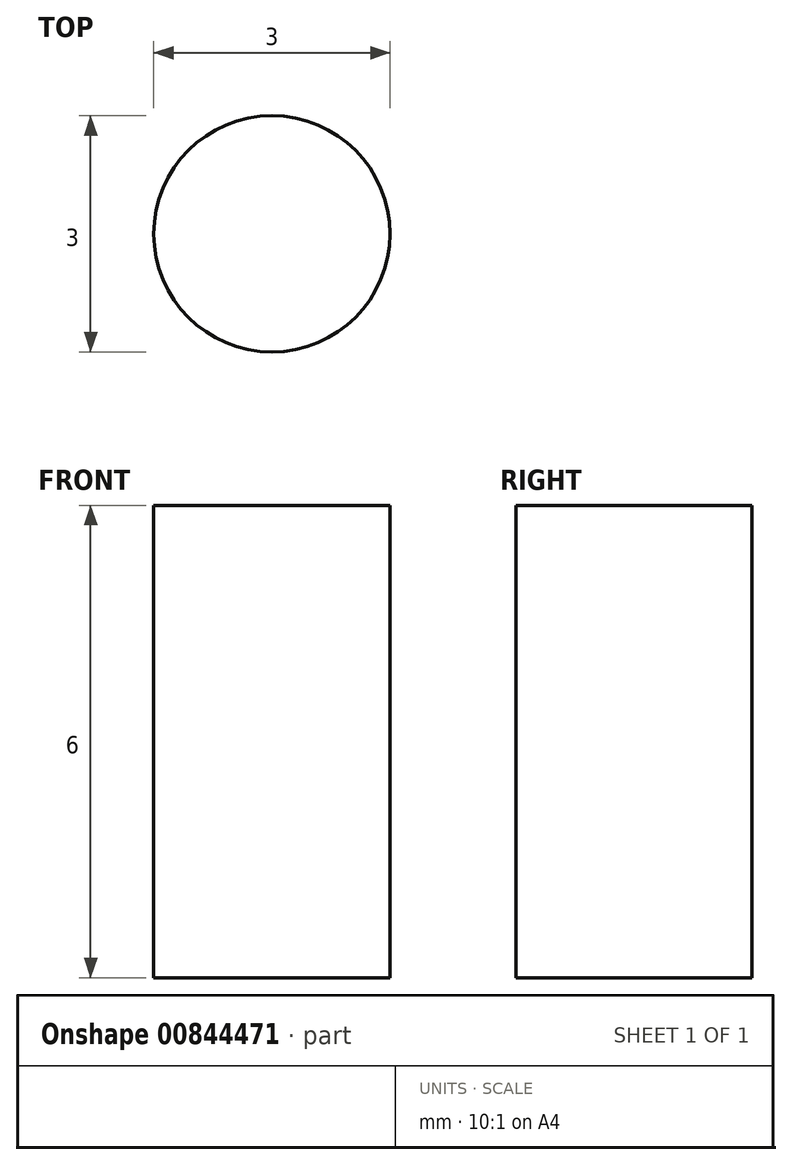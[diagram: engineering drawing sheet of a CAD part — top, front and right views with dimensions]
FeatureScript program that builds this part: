
annotation { "Feature Type Name" : "Feature", "Feature Type Description" : "" }
export const myFeature = defineFeature(function(context is Context, id is Id, definition is map)
    precondition{}
    {
        {
            var Q0;
            Q0=qCreatedBy(makeId("Top.planeOp"),FACE);
            var sketch = newSketch(context, id + "F0", { "sketchPlane" : qUnion([Q0])});
            skCircle(sketch, "E0", {"center": v(0, 0) * mm, "radius": 1.5 * mm});
            skSolve(sketch);
        }
        {
            var Q0;
            Q0 = qSketchRegion(id + "F0", true);
            extrude(context, id + "F1", {"entities" : qUnion([Q0]), "depth" : 6 * mm, "offsetDistance" : 25 * mm});
        }
    });
